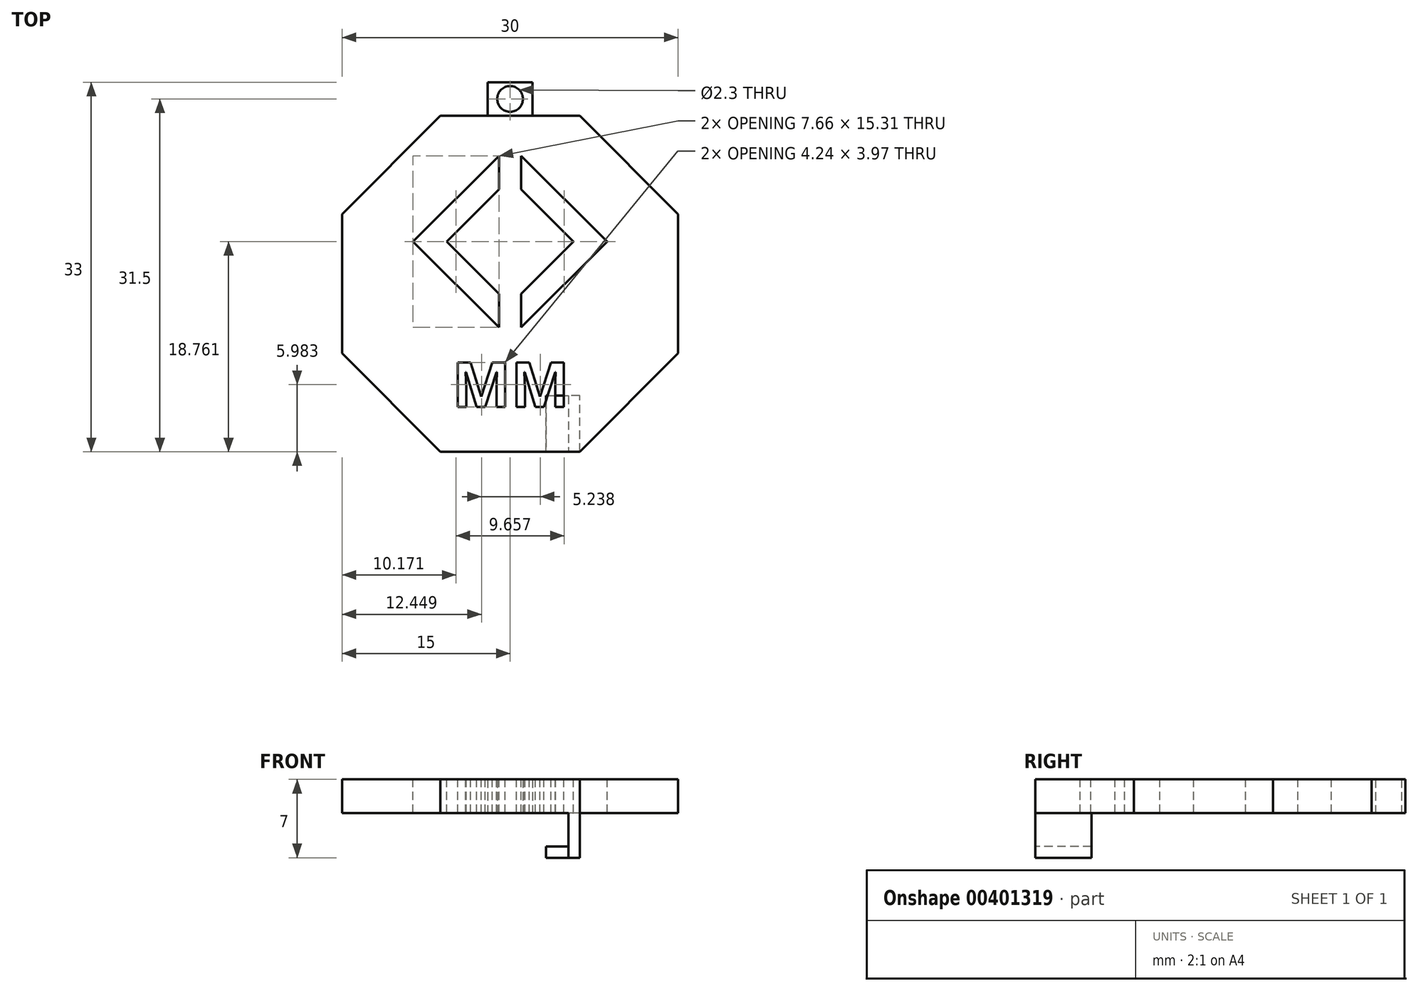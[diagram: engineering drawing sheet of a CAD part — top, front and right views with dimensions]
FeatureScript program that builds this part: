
annotation { "Feature Type Name" : "Feature", "Feature Type Description" : "" }
export const myFeature = defineFeature(function(context is Context, id is Id, definition is map)
    precondition{}
    {
        {
            var Q0;
            Q0=qCreatedBy(makeId("Top.planeOp"),FACE);
            var sketch = newSketch(context, id + "F0", { "sketchPlane" : qUnion([Q0])});
            skCircle(sketch, "E0.cCircle", {"center": v(0, 0) * mm, "radius": 15 * mm, "construction": true});
            skLineSegment(sketch, "E0.0", {"start": v(15, 6.21) * mm, "end": v(15, -6.21) * mm});
            skLineSegment(sketch, "E0.1", {"start": v(15, -6.21) * mm, "end": v(6.21, -15) * mm});
            skLineSegment(sketch, "E0.2", {"start": v(6.21, -15) * mm, "end": v(-6.21, -15) * mm});
            skLineSegment(sketch, "E0.3", {"start": v(-6.21, -15) * mm, "end": v(-15, -6.21) * mm});
            skLineSegment(sketch, "E0.4", {"start": v(-15, -6.21) * mm, "end": v(-15, 6.21) * mm});
            skLineSegment(sketch, "E0.5", {"start": v(-15, 6.21) * mm, "end": v(-6.21, 15) * mm});
            skLineSegment(sketch, "E0.6", {"start": v(-6.21, 15) * mm, "end": v(6.21, 15) * mm});
            skLineSegment(sketch, "E0.7", {"start": v(6.21, 15) * mm, "end": v(15, 6.21) * mm});
            skPoint(sketch, "E0.0.midPoint", {"position": v(15, 0) * mm});
            skLineSegment(sketch, "E1", {"start": v(0, 0) * mm, "end": v(-15, 0) * mm, "construction": true});
            skSolve(sketch);
        }
        {
            var Q0;
            Q0=qSketchRegion(id+"F0",true);
            extrude(context, id + "F1", {"entities" : qUnion([Q0]), "depth" : 3 * mm});
        }
        {
            var Q0;
            Q0=makeQuery(id+"F1.opExtrude","CAP_FACE",FACE,{"disambiguationData":[OSD([sQuery(id+"F0.wireOp",EDGE,"E0.0"),sQuery(id+"F0.wireOp",EDGE,"E0.1"),sQuery(id+"F0.wireOp",EDGE,"E0.2"),sQuery(id+"F0.wireOp",EDGE,"E0.3"),sQuery(id+"F0.wireOp",EDGE,"E0.4"),sQuery(id+"F0.wireOp",EDGE,"E0.5"),sQuery(id+"F0.wireOp",EDGE,"E0.6"),sQuery(id+"F0.wireOp",EDGE,"E0.7")])],"isStart":false});
            var sketch = newSketch(context, id + "F2", { "sketchPlane" : qUnion([Q0])});
            skText(sketch, "E2", { "text": "MM", "fontName": "OpenSans-Bold.ttf"});
            skArc(sketch, "E3.cCircle", {"start": v(2.83, 0.93) * mm, "mid": v(0, 7.76) * mm, "end": v(-2.83, 0.93) * mm, "construction": true});
            skLineSegment(sketch, "E3.0", {"start": v(5.66, 3.76) * mm, "end": v(1, -0.9) * mm});
            skLineSegment(sketch, "E3.2", {"start": v(-5.66, 3.76) * mm, "end": v(-1, 8.42) * mm});
            skLineSegment(sketch, "E3.3", {"start": v(1, 8.42) * mm, "end": v(5.66, 3.76) * mm});
            skPoint(sketch, "E3.0.midPoint", {"position": v(2.83, 0.93) * mm});
            skLineSegment(sketch, "E4", {"start": v(-5.66, 3.76) * mm, "end": v(0, 3.76) * mm, "construction": true});
            skLineSegment(sketch, "E5.1", {"start": v(8.66, 3.76) * mm, "end": v(1, -3.9) * mm});
            skLineSegment(sketch, "E5.3", {"start": v(-8.66, 3.76) * mm, "end": v(-1, 11.42) * mm});
            skPoint(sketch, "E5.0.midPoint", {"position": v(4.33, 8.1) * mm});
            skLineSegment(sketch, "E6", {"start": v(-8.66, 3.76) * mm, "end": v(-5.66, 3.76) * mm, "construction": true});
            skPoint(sketch, "E7.orphan", {"position": v(0, -1.9) * mm});
            skPoint(sketch, "E8.orphan", {"position": v(0, -4.9) * mm});
            skPoint(sketch, "E9.orphan", {"position": v(0.45, -660.17) * mm});
            skPoint(sketch, "E10.orphan", {"position": v(-0.45, -23.95) * mm});
            skLineSegment(sketch, "E11.trimOffspring", {"start": v(0, 3.76) * mm, "end": v(8.66, 3.76) * mm, "construction": true});
            skPoint(sketch, "E12.orphan", {"position": v(0, 9.42) * mm});
            skPoint(sketch, "E13.orphan", {"position": v(0, 12.42) * mm});
            skPoint(sketch, "E14.bottom.end.orphan", {"position": v(0.45, 31.48) * mm});
            skPoint(sketch, "E14.bottom.start.orphan", {"position": v(-0.45, 667.69) * mm});
            skPoint(sketch, "E15.firstSnap0", {"position": v(-10.6, -10.6) * mm});
            skPoint(sketch, "E15.secondSnap0", {"position": v(10.6, 10.6) * mm});
            skPoint(sketch, "E16.startSnap0", {"position": v(0.45, 11.37) * mm});
            skLineSegment(sketch, "E17", {"start": v(1, 11.42) * mm, "end": v(1, 8.42) * mm});
            skLineSegment(sketch, "E18", {"start": v(-1, 11.42) * mm, "end": v(-1, 8.42) * mm});
            skPoint(sketch, "E19.orphan", {"position": v(0.45, 12.87) * mm});
            skLineSegment(sketch, "E20.trimOffspring", {"start": v(1, 11.42) * mm, "end": v(8.66, 3.76) * mm});
            skPoint(sketch, "E21.trimOffspring.end.orphan", {"position": v(0.45, 9.87) * mm});
            skLineSegment(sketch, "E22.trimOffspring", {"start": v(-1, -0.9) * mm, "end": v(-5.66, 3.76) * mm});
            skLineSegment(sketch, "E23.trimOffspring", {"start": v(-1, -0.9) * mm, "end": v(-1, -3.9) * mm});
            skLineSegment(sketch, "E24.trimOffspring", {"start": v(1, -0.9) * mm, "end": v(1, -3.9) * mm});
            skLineSegment(sketch, "E25.trimOffspring", {"start": v(-1, -3.9) * mm, "end": v(-8.66, 3.76) * mm});
            const initialGuessF2  = {"E2": [-0.00517, -0.011, 1, 0, 0.004]};
            skSetInitialGuess(sketch, initialGuessF2);
            skSolve(sketch);
        }
        {
            var Q0;
            Q0=qSketchRegion(id+"F2",true);
            extrude(context, id + "F3", {"entities" : qUnion([Q0]), "operationType" : NewBodyOperationType.REMOVE, "endBound" : BoundingType.THROUGH_ALL, "oppositeDirection" : true, "depth" : 3 * mm});
        }
        {
            var Q0;
            Q0=makeQuery(id+"F1.opExtrude","CAP_FACE",FACE,{"disambiguationData":[OSD([sQuery(id+"F0.wireOp",EDGE,"E0.0"),sQuery(id+"F0.wireOp",EDGE,"E0.1"),sQuery(id+"F0.wireOp",EDGE,"E0.2"),sQuery(id+"F0.wireOp",EDGE,"E0.3"),sQuery(id+"F0.wireOp",EDGE,"E0.4"),sQuery(id+"F0.wireOp",EDGE,"E0.5"),sQuery(id+"F0.wireOp",EDGE,"E0.6"),sQuery(id+"F0.wireOp",EDGE,"E0.7")])],"isStart":true});
            var sketch = newSketch(context, id + "F4", { "sketchPlane" : qUnion([Q0])});
            skLineSegment(sketch, "E26.bottom", {"start": v(6.21, 15) * mm, "end": v(5.21, 15) * mm});
            skLineSegment(sketch, "E26.top", {"start": v(6.21, 10) * mm, "end": v(5.21, 10) * mm});
            skLineSegment(sketch, "E26.left", {"start": v(6.21, 15) * mm, "end": v(6.21, 10) * mm});
            skLineSegment(sketch, "E26.right", {"start": v(5.21, 15) * mm, "end": v(5.21, 10) * mm});
            skSolve(sketch);
        }
        {
            var Q0;
            Q0=qSketchRegion(id+"F4",true);
            extrude(context, id + "F5", {"entities" : qUnion([Q0]), "operationType" : NewBodyOperationType.ADD, "depth" : 4 * mm});
        }
        {
            var Q0;
            Q0=makeQuery(id+"F5.opExtrude","SWEPT_FACE",FACE,{"disambiguationData":[OSD([sQuery(id+"F4.wireOp",EDGE,"E26.right")])]});
            var sketch = newSketch(context, id + "F6", { "sketchPlane" : qUnion([Q0])});
            skLineSegment(sketch, "E27.bottom", {"start": v(10, -4) * mm, "end": v(15, -4) * mm});
            skLineSegment(sketch, "E27.top", {"start": v(10, -3) * mm, "end": v(15, -3) * mm});
            skLineSegment(sketch, "E27.left", {"start": v(10, -4) * mm, "end": v(10, -3) * mm});
            skLineSegment(sketch, "E27.right", {"start": v(15, -4) * mm, "end": v(15, -3) * mm});
            skSolve(sketch);
        }
        {
            var Q0;
            Q0=makeQuery(id+"F6.imprint","IMPRINT",FACE,{"disambiguationData":[TD([[makeQuery(id+"F6.imprint","IMPRINT",EDGE,{"derivedFrom":sQuery(id+"F6.wireOp",EDGE,"E27.bottom")}),-1.0]])]});
            var Q1;
            Q1=sQuery(id+"F6.wireOp",EDGE,"E27.top");
            var Q2;
            Q2=sQuery(id+"F6.wireOp",EDGE,"E27.bottom");
            var Q3;
            Q3=sQuery(id+"F6.wireOp",EDGE,"E27.right");
            var Q4;
            Q4=sQuery(id+"F6.wireOp",EDGE,"E27.left");
            extrude(context, id + "F7", {"entities" : qUnion([Q0]), "surfaceEntities" : qUnion([Q1, Q2, Q3, Q4]), "depth" : 2 * mm});
        }
        {
            var Q0;
            Q0=makeQuery(id+"F1.opExtrude","SWEPT_FACE",FACE,{"disambiguationData":[OSD([sQuery(id+"F0.wireOp",EDGE,"E0.6")])]});
            var sketch = newSketch(context, id + "F8", { "sketchPlane" : qUnion([Q0])});
            skLineSegment(sketch, "E28.bottom", {"start": v(2, 3) * mm, "end": v(-2, 3) * mm});
            skLineSegment(sketch, "E28.top", {"start": v(2, 0) * mm, "end": v(-2, 0) * mm});
            skLineSegment(sketch, "E28.left", {"start": v(2, 3) * mm, "end": v(2, 0) * mm});
            skLineSegment(sketch, "E28.right", {"start": v(-2, 3) * mm, "end": v(-2, 0) * mm});
            skPoint(sketch, "E28.middle", {"position": v(0, 1.5) * mm});
            skPoint(sketch, "E28.middle.positionSnap0", {"position": v(0, 3) * mm});
            skPoint(sketch, "E28.centerSnap0", {"position": v(0, 3) * mm});
            skSolve(sketch);
        }
        {
            var Q0;
            Q0=qSketchRegion(id+"F8",true);
            extrude(context, id + "F9", {"entities" : qUnion([Q0]), "depth" : 3 * mm});
        }
        {
            var Q0;
            Q0=makeQuery(id+"F9.opExtrude","SWEPT_FACE",FACE,{"disambiguationData":[OSD([sQuery(id+"F8.wireOp",EDGE,"E28.top")])]});
            var sketch = newSketch(context, id + "F10", { "sketchPlane" : qUnion([Q0])});
            skCircle(sketch, "E29", {"center": v(0, -16.5) * mm, "radius": 1.15 * mm});
            skLineSegment(sketch, "E30", {"start": v(0, -16.5) * mm, "end": v(0, -15) * mm, "construction": true});
            skLineSegment(sketch, "E31", {"start": v(0, -16.5) * mm, "end": v(0, -18) * mm, "construction": true});
            skSolve(sketch);
        }
        {
            var Q0;
            Q0=qSketchRegion(id+"F10",true);
            extrude(context, id + "F11", {"entities" : qUnion([Q0]), "operationType" : NewBodyOperationType.REMOVE, "endBound" : BoundingType.THROUGH_ALL, "oppositeDirection" : true, "depth" : 25 * mm});
        }
    });
